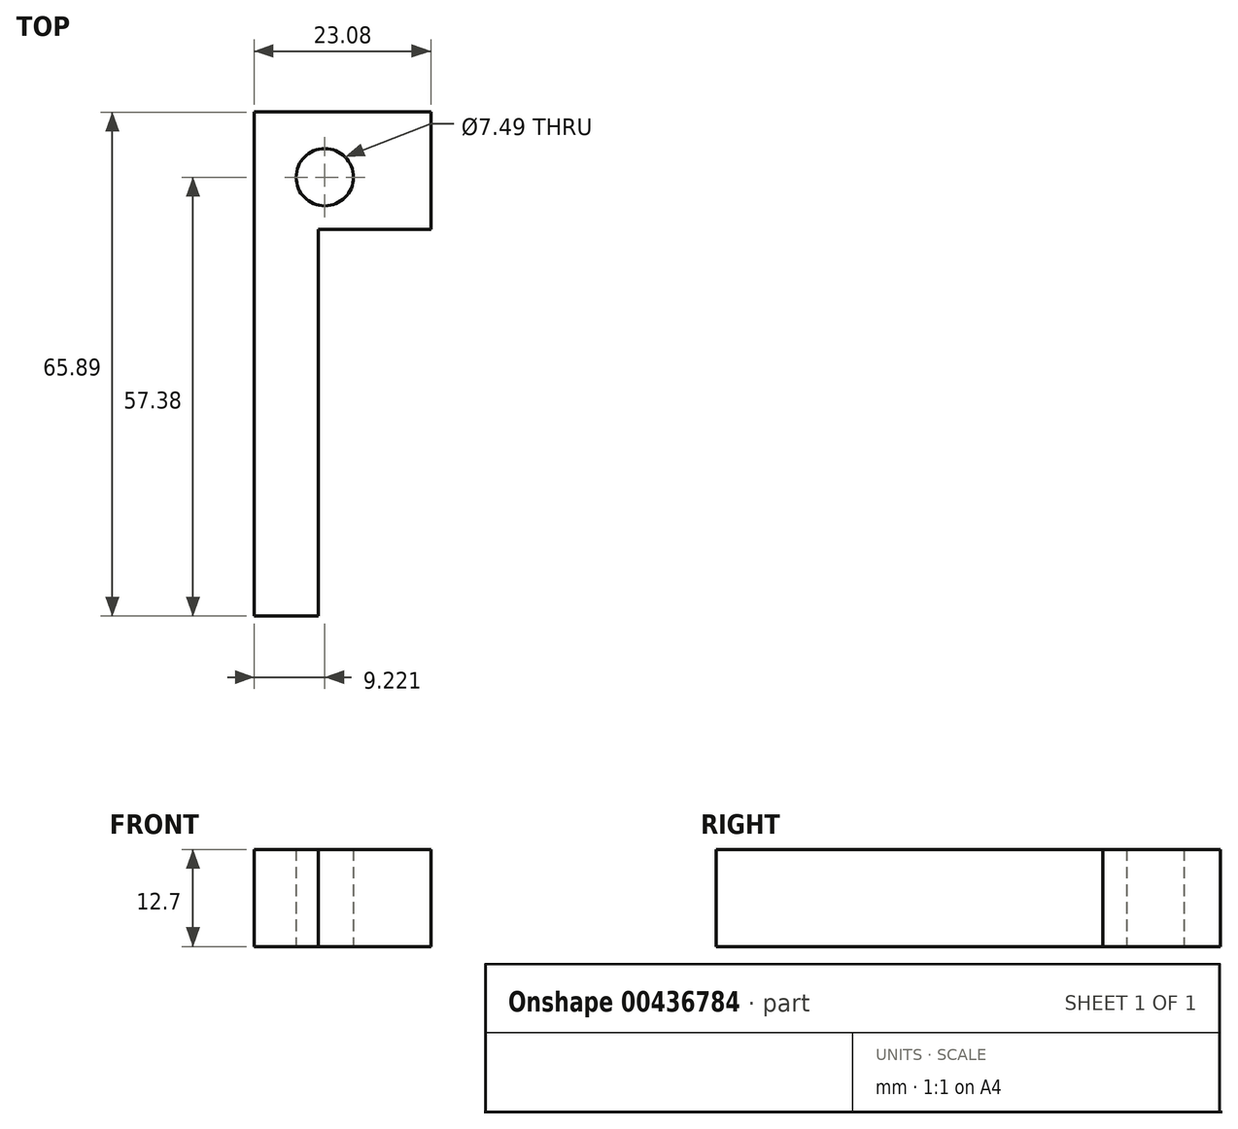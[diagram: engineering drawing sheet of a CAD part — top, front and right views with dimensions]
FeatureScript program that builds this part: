
annotation { "Feature Type Name" : "Feature", "Feature Type Description" : "" }
export const myFeature = defineFeature(function(context is Context, id is Id, definition is map)
    precondition{}
    {
        {
            var Q0;
            Q0=qCreatedBy(makeId("Top.planeOp"),FACE);
            var sketch = newSketch(context, id + "F0", { "sketchPlane" : qUnion([Q0])});
            skLineSegment(sketch, "E0", {"start": v(0, 0) * mm, "end": v(0, 29.68) * mm});
            skLineSegment(sketch, "E1", {"start": v(0, 29.68) * mm, "end": v(23.08, 29.68) * mm});
            skLineSegment(sketch, "E2", {"start": v(23.08, 29.68) * mm, "end": v(23.08, 14.36) * mm});
            skLineSegment(sketch, "E3", {"start": v(23.08, 14.36) * mm, "end": v(0, 14.36) * mm});
            skLineSegment(sketch, "E4", {"start": v(0, 14.36) * mm, "end": v(0, -12.92) * mm});
            skLineSegment(sketch, "E5", {"start": v(0, -12.92) * mm, "end": v(0, -36.21) * mm});
            skLineSegment(sketch, "E6", {"start": v(0, -36.21) * mm, "end": v(8.37, -36.21) * mm});
            skLineSegment(sketch, "E7", {"start": v(8.37, -36.21) * mm, "end": v(8.37, 14.36) * mm});
            skCircle(sketch, "E8", {"center": v(9.22, 21.17) * mm, "radius": 3.75 * mm});
            skSolve(sketch);
        }
        {
            var Q0;
            {var subQ0=sQuery(id+"F0.wireOp",EDGE,"E5");Q0=makeQuery(id+"F0.imprint","IMPRINT",FACE,{"disambiguationData":[TD([[makeQuery(id+"F0.imprint","IMPRINT",EDGE,{"derivedFrom":subQ0}),1.0]])]});}
            var Q1;
            {var subQ3=sQuery(id+"F0.wireOp",EDGE,"E0");Q1=makeQuery(id+"F0.imprint","IMPRINT",FACE,{"disambiguationData":[TD([[makeQuery(id+"F0.imprint","IMPRINT",EDGE,{"derivedFrom":subQ3}),-1.0]])]});}
            extrude(context, id + "F1", {"entities" : qUnion([Q0, Q1]), "depth" : 12.7 * mm});
        }
    });
